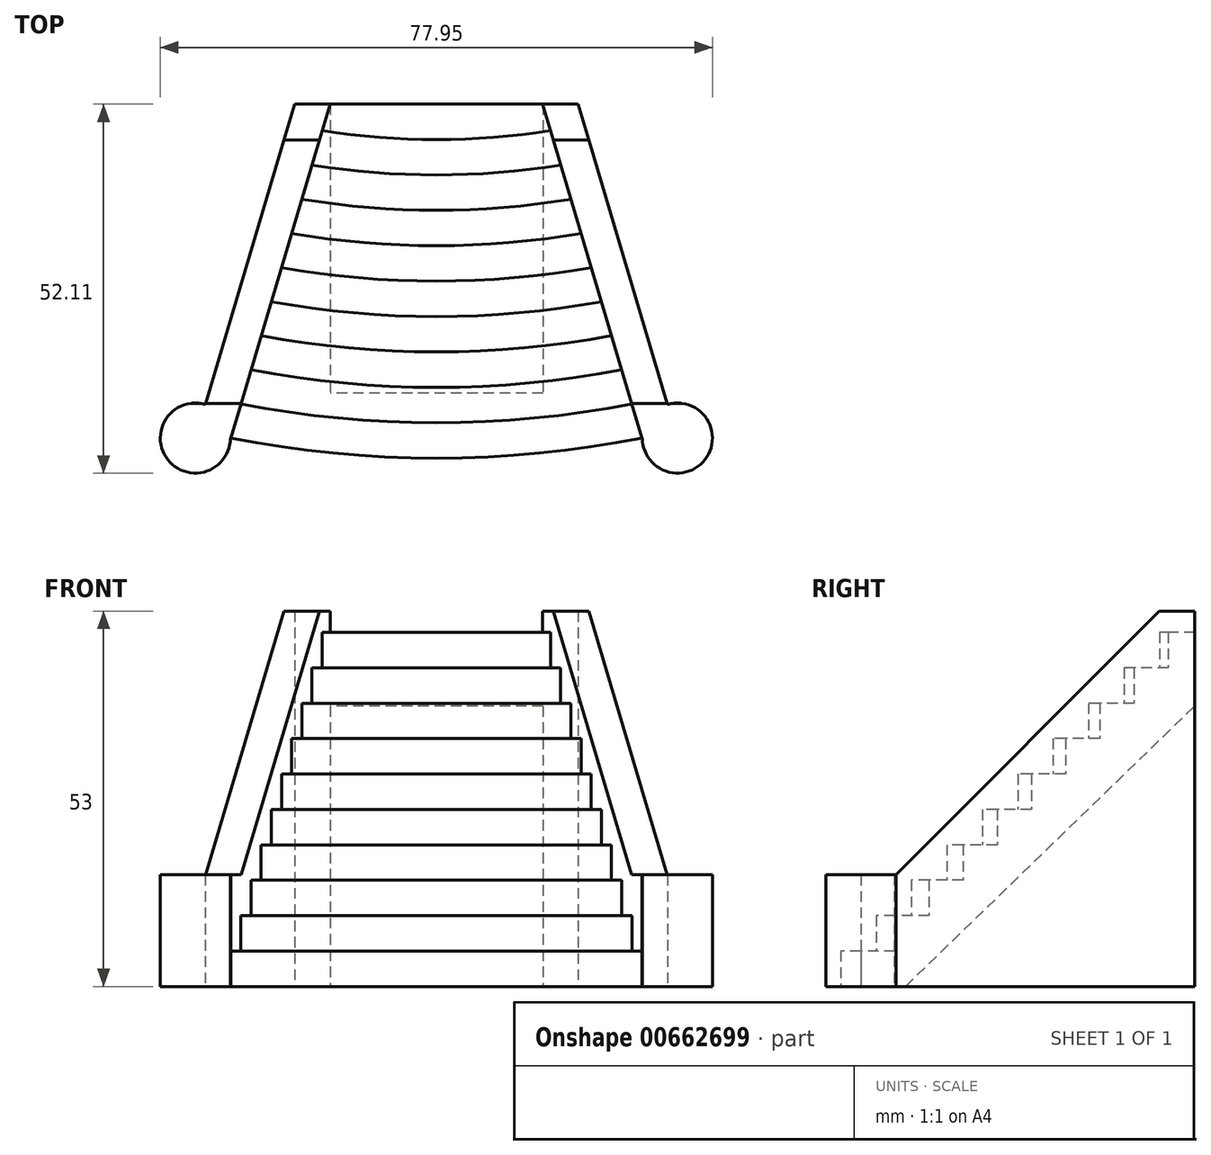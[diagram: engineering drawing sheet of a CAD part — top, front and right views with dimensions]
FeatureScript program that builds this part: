
annotation { "Feature Type Name" : "Feature", "Feature Type Description" : "" }
export const myFeature = defineFeature(function(context is Context, id is Id, definition is map)
    precondition{}
    {
        {
            var Q0;
            Q0=qCreatedBy(makeId("Top.planeOp"),FACE);
            var sketch = newSketch(context, id + "F0", { "sketchPlane" : qUnion([Q0])});
            skLineSegment(sketch, "E0", {"start": v(91.93, 0) * mm, "end": v(91.93, 200) * mm});
            skArc(sketch, "E1", {"start": v(33.88, -94.33) * mm, "mid": v(91.93, -100) * mm, "end": v(150, -94.33) * mm});
            skArc(sketch, "E2", {"start": v(36.74, -84.7) * mm, "mid": v(91.93, -90) * mm, "end": v(147.13, -84.7) * mm});
            skArc(sketch, "E3", {"start": v(39.6, -75.07) * mm, "mid": v(91.93, -80) * mm, "end": v(144.26, -75.07) * mm});
            skArc(sketch, "E4", {"start": v(42.47, -65.43) * mm, "mid": v(91.93, -70) * mm, "end": v(141.4, -65.43) * mm});
            skArc(sketch, "E5", {"start": v(45.34, -55.8) * mm, "mid": v(91.93, -60) * mm, "end": v(138.53, -55.8) * mm});
            skArc(sketch, "E6", {"start": v(48.2, -46.15) * mm, "mid": v(91.93, -50) * mm, "end": v(135.66, -46.15) * mm});
            skArc(sketch, "E7", {"start": v(51.08, -36.5) * mm, "mid": v(91.93, -40) * mm, "end": v(132.8, -36.5) * mm});
            skArc(sketch, "E8", {"start": v(53.95, -26.84) * mm, "mid": v(91.93, -30) * mm, "end": v(129.92, -26.84) * mm});
            skArc(sketch, "E9", {"start": v(56.82, -17.18) * mm, "mid": v(91.93, -20) * mm, "end": v(127.05, -17.18) * mm});
            skArc(sketch, "E10", {"start": v(59.7, -7.51) * mm, "mid": v(91.93, -10) * mm, "end": v(124.17, -7.51) * mm});
            skLineSegment(sketch, "E11", {"start": v(61.93, 0) * mm, "end": v(33.88, -94.33) * mm});
            skLineSegment(sketch, "E12.MirrorCS", {"start": v(121.93, 0) * mm, "end": v(150, -94.33) * mm});
            skLineSegment(sketch, "E13", {"start": v(61.93, 0) * mm, "end": v(121.93, 0) * mm});
            skLineSegment(sketch, "E14", {"start": v(61.93, 0) * mm, "end": v(51.93, 0) * mm});
            skLineSegment(sketch, "E15", {"start": v(51.93, 0) * mm, "end": v(26.7, -84.84) * mm});
            skLineSegment(sketch, "E16", {"start": v(33.77, -94.33) * mm, "end": v(33.88, -94.33) * mm});
            skArc(sketch, "E17", {"start": v(26.7, -84.84) * mm, "mid": v(15.94, -100.24) * mm, "end": v(33.77, -94.33) * mm});
            skLineSegment(sketch, "E18", {"start": v(91.93, 0) * mm, "end": v(91.93, -120.14) * mm});
            skPoint(sketch, "E18.endSnap0", {"position": v(91.93, -100) * mm});
            skLineSegment(sketch, "E19.MirrorCS", {"start": v(121.93, 0) * mm, "end": v(131.93, 0) * mm});
            skLineSegment(sketch, "E20.MirrorCS", {"start": v(131.93, 0) * mm, "end": v(157.17, -84.84) * mm});
            skArc(sketch, "E21.MirrorCS", {"start": v(157.17, -84.84) * mm, "mid": v(167.93, -100.24) * mm, "end": v(150.1, -94.33) * mm});
            skLineSegment(sketch, "E22", {"start": v(150.1, -94.33) * mm, "end": v(150, -94.33) * mm});
            skSolve(sketch);
        }
        {
            var Q0;
            {var subQ0=sQuery(id+"F0.wireOp",EDGE,"E1");Q0=makeQuery(id+"F0.imprint","IMPRINT",FACE,{"disambiguationData":[TD([[makeQuery(id+"F0.imprint","IMPRINT",EDGE,{"derivedFrom":subQ0}),1.0]])]});}
            extrude(context, id + "F1", {"entities" : qUnion([Q0]), "depth" : 10 * mm, "offsetDistance" : 25 * mm});
        }
        {
            var Q0;
            {var subQ0=sQuery(id+"F0.wireOp",EDGE,"E2");Q0=makeQuery(id+"F0.imprint","IMPRINT",FACE,{"disambiguationData":[TD([[makeQuery(id+"F0.imprint","IMPRINT",EDGE,{"derivedFrom":subQ0}),1.0]])]});}
            extrude(context, id + "F2", {"entities" : qUnion([Q0]), "operationType" : NewBodyOperationType.ADD, "depth" : 20 * mm, "offsetDistance" : 25 * mm});
        }
        {
            var Q0;
            {var subQ0=sQuery(id+"F0.wireOp",EDGE,"E3");Q0=makeQuery(id+"F0.imprint","IMPRINT",FACE,{"disambiguationData":[TD([[makeQuery(id+"F0.imprint","IMPRINT",EDGE,{"derivedFrom":subQ0}),1.0]])]});}
            extrude(context, id + "F3", {"entities" : qUnion([Q0]), "operationType" : NewBodyOperationType.ADD, "depth" : 30 * mm, "offsetDistance" : 25 * mm});
        }
        {
            var Q0;
            {var subQ0=sQuery(id+"F0.wireOp",EDGE,"E4");Q0=makeQuery(id+"F0.imprint","IMPRINT",FACE,{"disambiguationData":[TD([[makeQuery(id+"F0.imprint","IMPRINT",EDGE,{"derivedFrom":subQ0}),1.0]])]});}
            extrude(context, id + "F4", {"entities" : qUnion([Q0]), "operationType" : NewBodyOperationType.ADD, "depth" : 40 * mm, "offsetDistance" : 25 * mm});
        }
        {
            var Q0;
            {var subQ0=sQuery(id+"F0.wireOp",EDGE,"E5");Q0=makeQuery(id+"F0.imprint","IMPRINT",FACE,{"disambiguationData":[TD([[makeQuery(id+"F0.imprint","IMPRINT",EDGE,{"derivedFrom":subQ0}),1.0]])]});}
            extrude(context, id + "F5", {"entities" : qUnion([Q0]), "operationType" : NewBodyOperationType.ADD, "depth" : 50 * mm, "offsetDistance" : 25 * mm});
        }
        {
            var Q0;
            {var subQ0=sQuery(id+"F0.wireOp",EDGE,"E6");Q0=makeQuery(id+"F0.imprint","IMPRINT",FACE,{"disambiguationData":[TD([[makeQuery(id+"F0.imprint","IMPRINT",EDGE,{"derivedFrom":subQ0}),1.0]])]});}
            extrude(context, id + "F6", {"entities" : qUnion([Q0]), "operationType" : NewBodyOperationType.ADD, "depth" : 60 * mm, "offsetDistance" : 25 * mm});
        }
        {
            var Q0;
            {var subQ0=sQuery(id+"F0.wireOp",EDGE,"E7");Q0=makeQuery(id+"F0.imprint","IMPRINT",FACE,{"disambiguationData":[TD([[makeQuery(id+"F0.imprint","IMPRINT",EDGE,{"derivedFrom":subQ0}),1.0]])]});}
            extrude(context, id + "F7", {"entities" : qUnion([Q0]), "operationType" : NewBodyOperationType.ADD, "depth" : 70 * mm, "offsetDistance" : 25 * mm});
        }
        {
            var Q0;
            {var subQ0=sQuery(id+"F0.wireOp",EDGE,"E8");Q0=makeQuery(id+"F0.imprint","IMPRINT",FACE,{"disambiguationData":[TD([[makeQuery(id+"F0.imprint","IMPRINT",EDGE,{"derivedFrom":subQ0}),1.0]])]});}
            extrude(context, id + "F8", {"entities" : qUnion([Q0]), "operationType" : NewBodyOperationType.ADD, "depth" : 80 * mm, "offsetDistance" : 25 * mm});
        }
        {
            var Q0;
            {var subQ0=sQuery(id+"F0.wireOp",EDGE,"E9");Q0=makeQuery(id+"F0.imprint","IMPRINT",FACE,{"disambiguationData":[TD([[makeQuery(id+"F0.imprint","IMPRINT",EDGE,{"derivedFrom":subQ0}),1.0]])]});}
            extrude(context, id + "F9", {"entities" : qUnion([Q0]), "operationType" : NewBodyOperationType.ADD, "depth" : 90 * mm, "offsetDistance" : 25 * mm});
        }
        {
            var Q0;
            {var subQ5=sQuery(id+"F0.wireOp",EDGE,"E10");Q0=makeQuery(id+"F0.imprint","IMPRINT",FACE,{"disambiguationData":[TD([[makeQuery(id+"F0.imprint","IMPRINT",EDGE,{"derivedFrom":subQ5}),1.0]])]});}
            extrude(context, id + "F10", {"entities" : qUnion([Q0]), "operationType" : NewBodyOperationType.ADD, "depth" : 100 * mm, "offsetDistance" : 25 * mm});
        }
        {
            var Q0;
            {var subQ9=sQuery(id+"F0.wireOp",EDGE,"E14");Q0=makeQuery(id+"F0.imprint","IMPRINT",FACE,{"disambiguationData":[TD([[makeQuery(id+"F0.imprint","IMPRINT",EDGE,{"derivedFrom":subQ9}),1.0]])]});}
            var Q1;
            {var subQ9=sQuery(id+"F0.wireOp",EDGE,"E19.MirrorCS");Q1=makeQuery(id+"F0.imprint","IMPRINT",FACE,{"disambiguationData":[TD([[makeQuery(id+"F0.imprint","IMPRINT",EDGE,{"derivedFrom":subQ9}),-1.0]])]});}
            extrude(context, id + "F11", {"entities" : qUnion([Q0, Q1]), "operationType" : NewBodyOperationType.ADD, "depth" : 106 * mm, "offsetDistance" : 25 * mm});
        }
        {
            var Q0;
            Q0=qCreatedBy(makeId("Right.planeOp"),FACE);
            var sketch = newSketch(context, id + "F12", { "sketchPlane" : qUnion([Q0])});
            skLineSegment(sketch, "E23", {"start": v(0, 106.08) * mm, "end": v(-10, 106.08) * mm});
            skLineSegment(sketch, "E24", {"start": v(-10, 106.08) * mm, "end": v(-84.52, 31.53) * mm});
            skLineSegment(sketch, "E25", {"start": v(-84.52, 31.53) * mm, "end": v(-105.49, 31.53) * mm});
            skLineSegment(sketch, "E26", {"start": v(-105.49, 31.53) * mm, "end": v(-105.49, 106.08) * mm});
            skLineSegment(sketch, "E27", {"start": v(-105.49, 106.08) * mm, "end": v(-10, 106.08) * mm});
            skLineSegment(sketch, "E28", {"start": v(-81.64, 0) * mm, "end": v(0, 79.2) * mm});
            skLineSegment(sketch, "E29", {"start": v(0, 79.2) * mm, "end": v(0, 0) * mm});
            skLineSegment(sketch, "E30", {"start": v(0, 0) * mm, "end": v(-81.64, 0) * mm});
            skSolve(sketch);
        }
        {
            var Q0;
            Q0=makeQuery(id+"F12.imprint","IMPRINT",FACE,{"disambiguationData":[TD([[makeQuery(id+"F12.imprint","IMPRINT",EDGE,{"derivedFrom":sQuery(id+"F12.wireOp",EDGE,"E24")}),-1.0]])]});
            extrude(context, id + "F13", {"entities" : qUnion([Q0]), "operationType" : NewBodyOperationType.REMOVE, "depth" : 200 * mm, "offsetDistance" : 25 * mm});
        }
        {
            var Q0;
            Q0=makeQuery(id+"F12.imprint","IMPRINT",FACE,{"disambiguationData":[TD([[makeQuery(id+"F12.imprint","IMPRINT",EDGE,{"derivedFrom":sQuery(id+"F12.wireOp",EDGE,"E28")}),-1.0]])]});
            extrude(context, id + "F14", {"entities" : qUnion([Q0]), "operationType" : NewBodyOperationType.REMOVE, "depth" : 122 * mm, "offsetDistance" : 25 * mm, "hasSecondDirection" : true, "secondDirectionOppositeDirection" : false, "secondDirectionDepth" : 62 * mm});
        }
        {
            var Q0;
            Q0=makeQuery(id+"F1.opExtrude","SWEPT_BODY",BODY,{"disambiguationData":[OSD([sQuery(id+"F0.wireOp",EDGE,"E1"),sQuery(id+"F0.wireOp",EDGE,"E2"),sQuery(id+"F0.wireOp",EDGE,"E11"),sQuery(id+"F0.wireOp",EDGE,"E12.MirrorCS")])]});
            var Q1;
            Q1=sQuery(id+"F0.wireOp",VERTEX,"E15.start");
            transform(context, id + "F15", {"entities" : qUnion([Q0]), "transformType" : TransformType.SCALE_UNIFORMLY, "scale" : .5, "scalePoint" : qUnion([Q1]), "makeCopy" : false});
        }
    });
